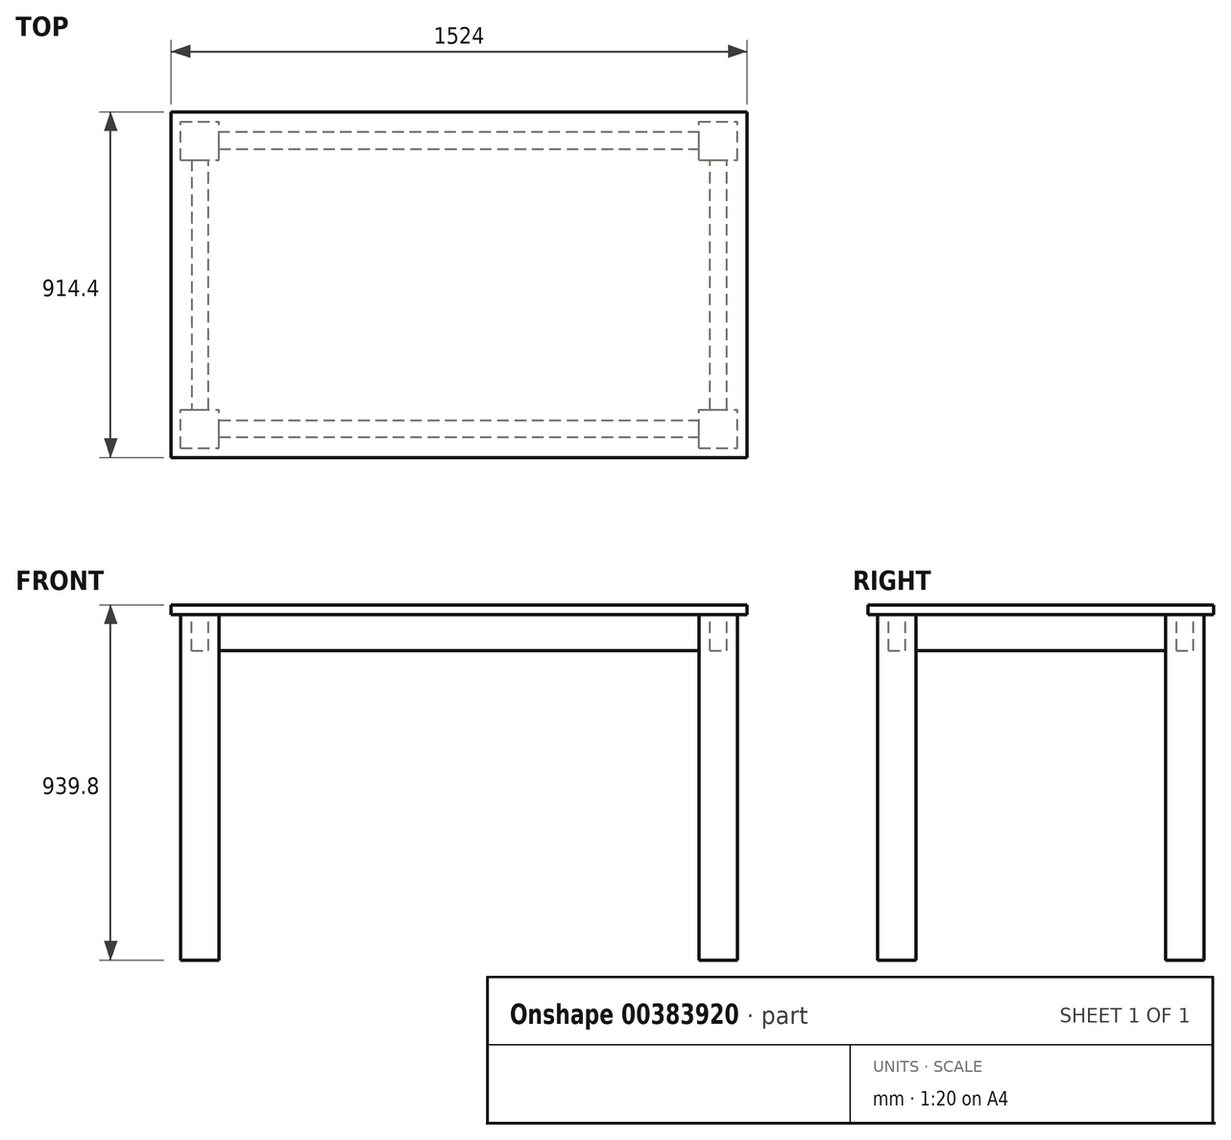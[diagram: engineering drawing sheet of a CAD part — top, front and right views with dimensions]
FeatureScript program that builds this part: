
annotation { "Feature Type Name" : "Feature", "Feature Type Description" : "" }
export const myFeature = defineFeature(function(context is Context, id is Id, definition is map)
    precondition{}
    {
        {
            var Q0;
            Q0=qCreatedBy(makeId("Top.planeOp"),FACE);
            var sketch = newSketch(context, id + "F0", { "sketchPlane" : qUnion([Q0])});
            skLineSegment(sketch, "E0.bottom", {"start": v(-761.65, 556.48) * mm, "end": v(762.35, 556.48) * mm});
            skLineSegment(sketch, "E0.top", {"start": v(-761.65, -357.92) * mm, "end": v(762.35, -357.92) * mm});
            skLineSegment(sketch, "E0.left", {"start": v(-761.65, 556.48) * mm, "end": v(-761.65, -357.92) * mm});
            skLineSegment(sketch, "E0.right", {"start": v(762.35, 556.48) * mm, "end": v(762.35, -357.92) * mm});
            skSolve(sketch);
        }
        {
            var Q0;
            Q0=makeQuery(id+"F0.imprint","IMPRINT",FACE,{"disambiguationData":[TD([[makeQuery(id+"F0.imprint","IMPRINT",EDGE,{"derivedFrom":sQuery(id+"F0.wireOp",EDGE,"E0.bottom")}),-1.0]])]});
            extrude(context, id + "F1", {"entities" : qUnion([Q0]), "depth" : 25.4 * mm});
        }
        {
            var Q0;
            Q0=makeQuery(id+"F1.opExtrude","CAP_FACE",FACE,{"disambiguationData":[OSD([sQuery(id+"F0.wireOp",EDGE,"E0.bottom"),sQuery(id+"F0.wireOp",EDGE,"E0.top"),sQuery(id+"F0.wireOp",EDGE,"E0.left"),sQuery(id+"F0.wireOp",EDGE,"E0.right")])],"isStart":true});
            var sketch = newSketch(context, id + "F2", { "sketchPlane" : qUnion([Q0])});
            skLineSegment(sketch, "E1.bottom", {"start": v(-736.25, 332.52) * mm, "end": v(-634.65, 332.52) * mm});
            skLineSegment(sketch, "E1.top", {"start": v(-736.25, 230.92) * mm, "end": v(-634.65, 230.92) * mm});
            skLineSegment(sketch, "E1.left", {"start": v(-736.25, 332.52) * mm, "end": v(-736.25, 230.92) * mm});
            skLineSegment(sketch, "E1.right", {"start": v(-634.65, 332.52) * mm, "end": v(-634.65, 230.92) * mm});
            skLineSegment(sketch, "E2.bottom", {"start": v(635.35, 332.52) * mm, "end": v(736.95, 332.52) * mm});
            skLineSegment(sketch, "E2.top", {"start": v(635.35, 230.92) * mm, "end": v(736.95, 230.92) * mm});
            skLineSegment(sketch, "E2.left", {"start": v(635.35, 332.52) * mm, "end": v(635.35, 230.92) * mm});
            skLineSegment(sketch, "E2.right", {"start": v(736.95, 332.52) * mm, "end": v(736.95, 230.92) * mm});
            skLineSegment(sketch, "E3.bottom", {"start": v(-736.25, -429.48) * mm, "end": v(-634.65, -429.48) * mm});
            skLineSegment(sketch, "E3.top", {"start": v(-736.25, -531.08) * mm, "end": v(-634.65, -531.08) * mm});
            skLineSegment(sketch, "E3.left", {"start": v(-736.25, -429.48) * mm, "end": v(-736.25, -531.08) * mm});
            skLineSegment(sketch, "E3.right", {"start": v(-634.65, -429.48) * mm, "end": v(-634.65, -531.08) * mm});
            skLineSegment(sketch, "E4.bottom", {"start": v(635.35, -429.48) * mm, "end": v(736.95, -429.48) * mm});
            skLineSegment(sketch, "E4.top", {"start": v(635.35, -531.08) * mm, "end": v(736.95, -531.08) * mm});
            skLineSegment(sketch, "E4.left", {"start": v(635.35, -429.48) * mm, "end": v(635.35, -531.08) * mm});
            skLineSegment(sketch, "E4.right", {"start": v(736.95, -429.48) * mm, "end": v(736.95, -531.08) * mm});
            skSolve(sketch);
        }
        {
            var Q0;
            Q0=makeQuery(id+"F2.imprint","IMPRINT",FACE,{"disambiguationData":[TD([[makeQuery(id+"F2.imprint","IMPRINT",EDGE,{"derivedFrom":sQuery(id+"F2.wireOp",EDGE,"E1.bottom")}),-1.0]])]});
            var Q1;
            Q1=makeQuery(id+"F2.imprint","IMPRINT",FACE,{"disambiguationData":[TD([[makeQuery(id+"F2.imprint","IMPRINT",EDGE,{"derivedFrom":sQuery(id+"F2.wireOp",EDGE,"E3.bottom")}),-1.0]])]});
            var Q2;
            Q2=makeQuery(id+"F2.imprint","IMPRINT",FACE,{"disambiguationData":[TD([[makeQuery(id+"F2.imprint","IMPRINT",EDGE,{"derivedFrom":sQuery(id+"F2.wireOp",EDGE,"E4.bottom")}),-1.0]])]});
            var Q3;
            Q3=makeQuery(id+"F2.imprint","IMPRINT",FACE,{"disambiguationData":[TD([[makeQuery(id+"F2.imprint","IMPRINT",EDGE,{"derivedFrom":sQuery(id+"F2.wireOp",EDGE,"E2.bottom")}),-1.0]])]});
            extrude(context, id + "F3", {"entities" : qUnion([Q0, Q1, Q2, Q3]), "depth" : 914.4 * mm});
        }
        {
            var Q0;
            Q0=makeQuery(id+"F1.opExtrude","CAP_FACE",FACE,{"disambiguationData":[OSD([sQuery(id+"F0.wireOp",EDGE,"E0.bottom"),sQuery(id+"F0.wireOp",EDGE,"E0.top"),sQuery(id+"F0.wireOp",EDGE,"E0.left"),sQuery(id+"F0.wireOp",EDGE,"E0.right")])],"isStart":true});
            var sketch = newSketch(context, id + "F4", { "sketchPlane" : qUnion([Q0])});
            skLineSegment(sketch, "E5", {"start": v(-634.65, 303.94) * mm, "end": v(635.35, 303.94) * mm});
            skLineSegment(sketch, "E6", {"start": v(-634.65, 259.5) * mm, "end": v(635.35, 259.5) * mm});
            skLineSegment(sketch, "E7", {"start": v(635.35, 281.72) * mm, "end": v(-634.65, 281.72) * mm, "construction": true});
            skLineSegment(sketch, "E8.0", {"start": v(-634.65, 332.52) * mm, "end": v(-634.65, 230.92) * mm});
            skLineSegment(sketch, "E9.0", {"start": v(635.35, 332.52) * mm, "end": v(635.35, 230.92) * mm});
            skLineSegment(sketch, "E10.0", {"start": v(635.35, 230.92) * mm, "end": v(736.95, 230.92) * mm});
            skLineSegment(sketch, "E11.0", {"start": v(-736.25, 230.92) * mm, "end": v(-634.65, 230.92) * mm});
            skLineSegment(sketch, "E12.0", {"start": v(-736.25, -429.48) * mm, "end": v(-634.65, -429.48) * mm});
            skLineSegment(sketch, "E13.0", {"start": v(-634.65, -429.48) * mm, "end": v(-634.65, -531.08) * mm});
            skLineSegment(sketch, "E14.0", {"start": v(635.35, -429.48) * mm, "end": v(635.35, -531.08) * mm});
            skLineSegment(sketch, "E15.0", {"start": v(635.35, -429.48) * mm, "end": v(736.95, -429.48) * mm});
            skLineSegment(sketch, "E16", {"start": v(708.38, 230.92) * mm, "end": v(708.38, -429.48) * mm});
            skLineSegment(sketch, "E17", {"start": v(686.15, -429.48) * mm, "end": v(686.15, 230.92) * mm, "construction": true});
            skLineSegment(sketch, "E18", {"start": v(663.93, 230.92) * mm, "end": v(663.93, -429.48) * mm});
            skLineSegment(sketch, "E19", {"start": v(635.35, -480.28) * mm, "end": v(-634.65, -480.28) * mm, "construction": true});
            skLineSegment(sketch, "E20", {"start": v(-685.45, 230.92) * mm, "end": v(-685.45, -429.48) * mm, "construction": true});
            skLineSegment(sketch, "E21", {"start": v(635.35, -502.5) * mm, "end": v(-634.65, -502.5) * mm});
            skLineSegment(sketch, "E22", {"start": v(-634.65, -458.06) * mm, "end": v(635.35, -458.06) * mm});
            skLineSegment(sketch, "E23", {"start": v(-663.22, 230.92) * mm, "end": v(-663.22, -429.48) * mm});
            skLineSegment(sketch, "E24", {"start": v(-707.67, -429.48) * mm, "end": v(-707.67, 230.92) * mm});
            skSolve(sketch);
        }
        {
            var Q0;
            {var subQ0=sQuery(id+"F4.wireOp",EDGE,"E5");Q0=makeQuery(id+"F4.imprint","IMPRINT",FACE,{"disambiguationData":[TD([[makeQuery(id+"F4.imprint","IMPRINT",EDGE,{"derivedFrom":subQ0}),-1.0]])]});}
            var Q1;
            {var subQ0=sQuery(id+"F4.wireOp",EDGE,"E16");Q1=makeQuery(id+"F4.imprint","IMPRINT",FACE,{"disambiguationData":[TD([[makeQuery(id+"F4.imprint","IMPRINT",EDGE,{"derivedFrom":subQ0}),-1.0]])]});}
            var Q2;
            {var subQ0=sQuery(id+"F4.wireOp",EDGE,"E21");Q2=makeQuery(id+"F4.imprint","IMPRINT",FACE,{"disambiguationData":[TD([[makeQuery(id+"F4.imprint","IMPRINT",EDGE,{"derivedFrom":subQ0}),-1.0]])]});}
            var Q3;
            {var subQ0=sQuery(id+"F4.wireOp",EDGE,"E23");Q3=makeQuery(id+"F4.imprint","IMPRINT",FACE,{"disambiguationData":[TD([[makeQuery(id+"F4.imprint","IMPRINT",EDGE,{"derivedFrom":subQ0}),-1.0]])]});}
            extrude(context, id + "F5", {"entities" : qUnion([Q0, Q1, Q2, Q3]), "depth" : 95.25 * mm});
        }
    });
